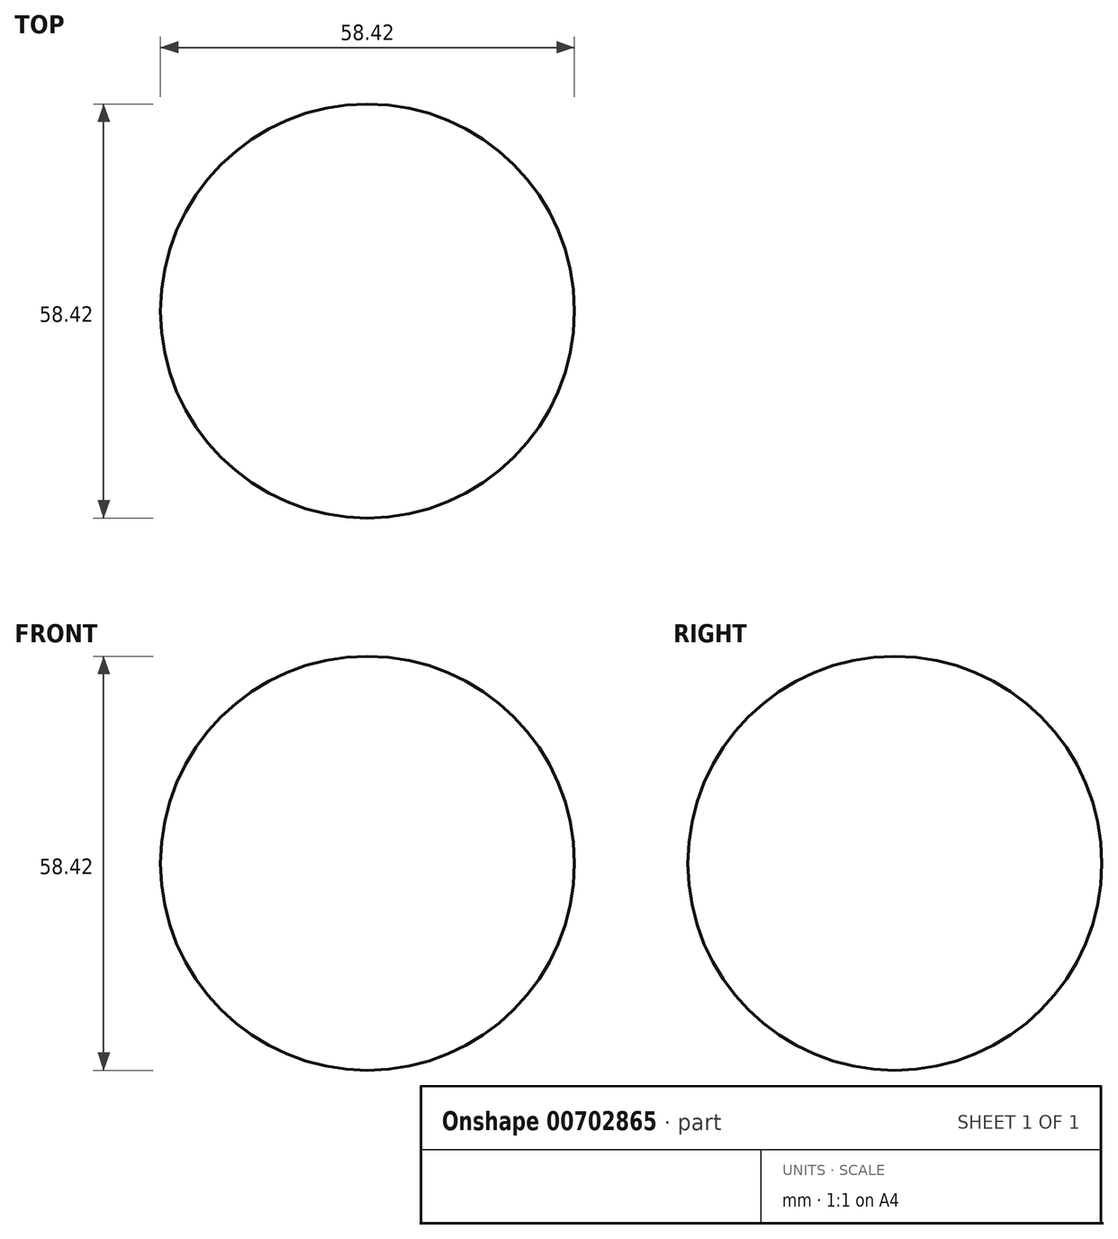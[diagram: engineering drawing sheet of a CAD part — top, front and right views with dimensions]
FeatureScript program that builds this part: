
annotation { "Feature Type Name" : "Feature", "Feature Type Description" : "" }
export const myFeature = defineFeature(function(context is Context, id is Id, definition is map)
    precondition{}
    {
        {
            var Q0;
            Q0=qCreatedBy(makeId("Front.planeOp"),FACE);
            var sketch = newSketch(context, id + "F0", { "sketchPlane" : qUnion([Q0])});
            skCircle(sketch, "E0", {"center": v(6.53, 0) * mm, "radius": 29.21 * mm});
            skLineSegment(sketch, "E1", {"start": v(6.53, 0) * mm, "end": v(6.53, 29.21) * mm});
            skLineSegment(sketch, "E2", {"start": v(6.53, 0) * mm, "end": v(6.53, -29.21) * mm});
            skSolve(sketch);
        }
        {
            var Q0;
            {var subQ0=sQuery(id+"F0.wireOp",EDGE,"E1");Q0=makeQuery(id+"F0.imprint","IMPRINT",FACE,{"disambiguationData":[TD([[makeQuery(id+"F0.imprint","IMPRINT",EDGE,{"derivedFrom":subQ0}),-1.0]])]});}
            var Q1;
            Q1=sQuery(id+"F0.wireOp",EDGE,"E1");
            revolve(context, id + "F1", {"surfaceOperationType" : NewSurfaceOperationType.NEW, "entities" : qUnion([Q0]), "axis" : qUnion([Q1]), "revolveType" : RevolveType.SYMMETRIC, "angle" : 360 * degree});
        }
    });
